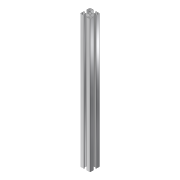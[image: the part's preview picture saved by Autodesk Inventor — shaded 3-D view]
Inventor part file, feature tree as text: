
AUTODESK INVENTOR PART (.ipt)
format: ipt  version: 2019 (Build 230136000, 136)  size: 308,736 bytes
history: native  units: mm
features: other x4, extrude x1, sketch x1, reference x1
ambient origin geometry x8: Origin, YZ Plane, XZ Plane, XY Plane, X Axis, Y Axis, Z Axis, Center Point
bodies: Body1 (feature_tree)
feature tree (7):
  other  "솔리드1"
  extrude  "돌출1"  Depth=400.0mm TaperAngle=0.0deg
  sketch  "스케치1"
  reference  "참조1"
  other  "<userpath>\Documents\Inventor\Projects\2019_CapstoneDesign\Body.iam"
  other  "Body.iam"
  other  "Propile_800:1"
